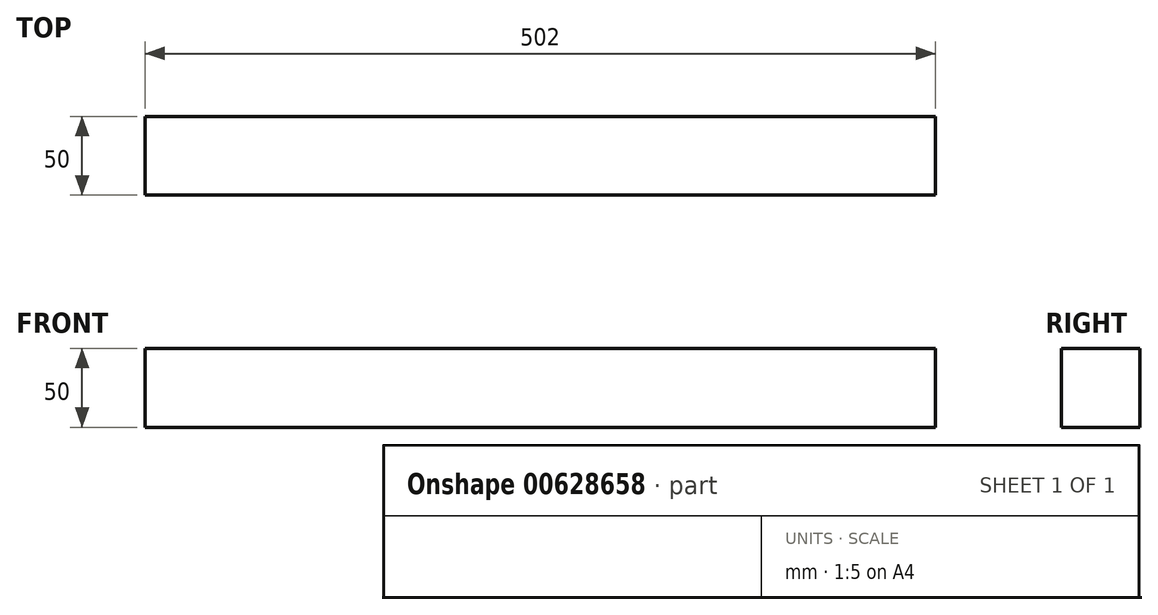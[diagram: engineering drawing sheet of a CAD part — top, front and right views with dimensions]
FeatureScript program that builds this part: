
annotation { "Feature Type Name" : "Feature", "Feature Type Description" : "" }
export const myFeature = defineFeature(function(context is Context, id is Id, definition is map)
    precondition{}
    {
        {
            var Q0;
            Q0=qCreatedBy(makeId("Right.planeOp"),FACE);
            var sketch = newSketch(context, id + "F0", { "sketchPlane" : qUnion([Q0])});
            skLineSegment(sketch, "E0.bottom", {"start": v(-25, 25) * mm, "end": v(25, 25) * mm});
            skLineSegment(sketch, "E0.top", {"start": v(-25, -25) * mm, "end": v(25, -25) * mm});
            skLineSegment(sketch, "E0.left", {"start": v(-25, 25) * mm, "end": v(-25, -25) * mm});
            skLineSegment(sketch, "E0.right", {"start": v(25, 25) * mm, "end": v(25, -25) * mm});
            skPoint(sketch, "E0.middle", {"position": v(0, 0) * mm});
            skSolve(sketch);
        }
        {
            var Q0;
            Q0=makeQuery(id+"F0.imprint","IMPRINT",FACE,{"disambiguationData":[TD([[makeQuery(id+"F0.imprint","IMPRINT",EDGE,{"derivedFrom":sQuery(id+"F0.wireOp",EDGE,"E0.bottom")}),-1.0]])]});
            extrude(context, id + "F1", {"entities" : qUnion([Q0]), "endBound" : BoundingType.SYMMETRIC, "depth" : 502 * mm, "offsetDistance" : 25 * mm});
        }
    });
